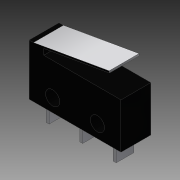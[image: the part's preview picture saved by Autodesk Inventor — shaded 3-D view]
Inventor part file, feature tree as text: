
AUTODESK INVENTOR PART (.ipt)
format: ipt  version: 2015 (Build 190159000, 159)  size: 124,416 bytes
history: native  units: in
note: dims shown in document units (in); Inventor stores cm internally (conversion verified against a paired STEP export)
features: extrude x2, sketch x2
ambient origin geometry x8: Origin, YZ Plane, XZ Plane, XY Plane, X Axis, Y Axis, Z Axis, Center Point
bodies: Solid1 (feature_tree)
feature tree (4):
  extrude  "Extrusion1"  Depth=0.1018in
  extrude  "Extrusion2"  Depth=0.015in
  sketch  "Sketch1"  dims[d2=0.0843in d3=0.1018in]
  sketch  "Sketch3"  dims[d4=0.385in d5=0.5815in d7=0.015in d8=0.0687in d9=0.78in d11=0.435in d12=0.254in d13=0.0in d16=0.12in d17=0.38in d18=0.11in d19=0.025in d20=0.025in d21=0.15in d22=0.15in d23=0.0in]
